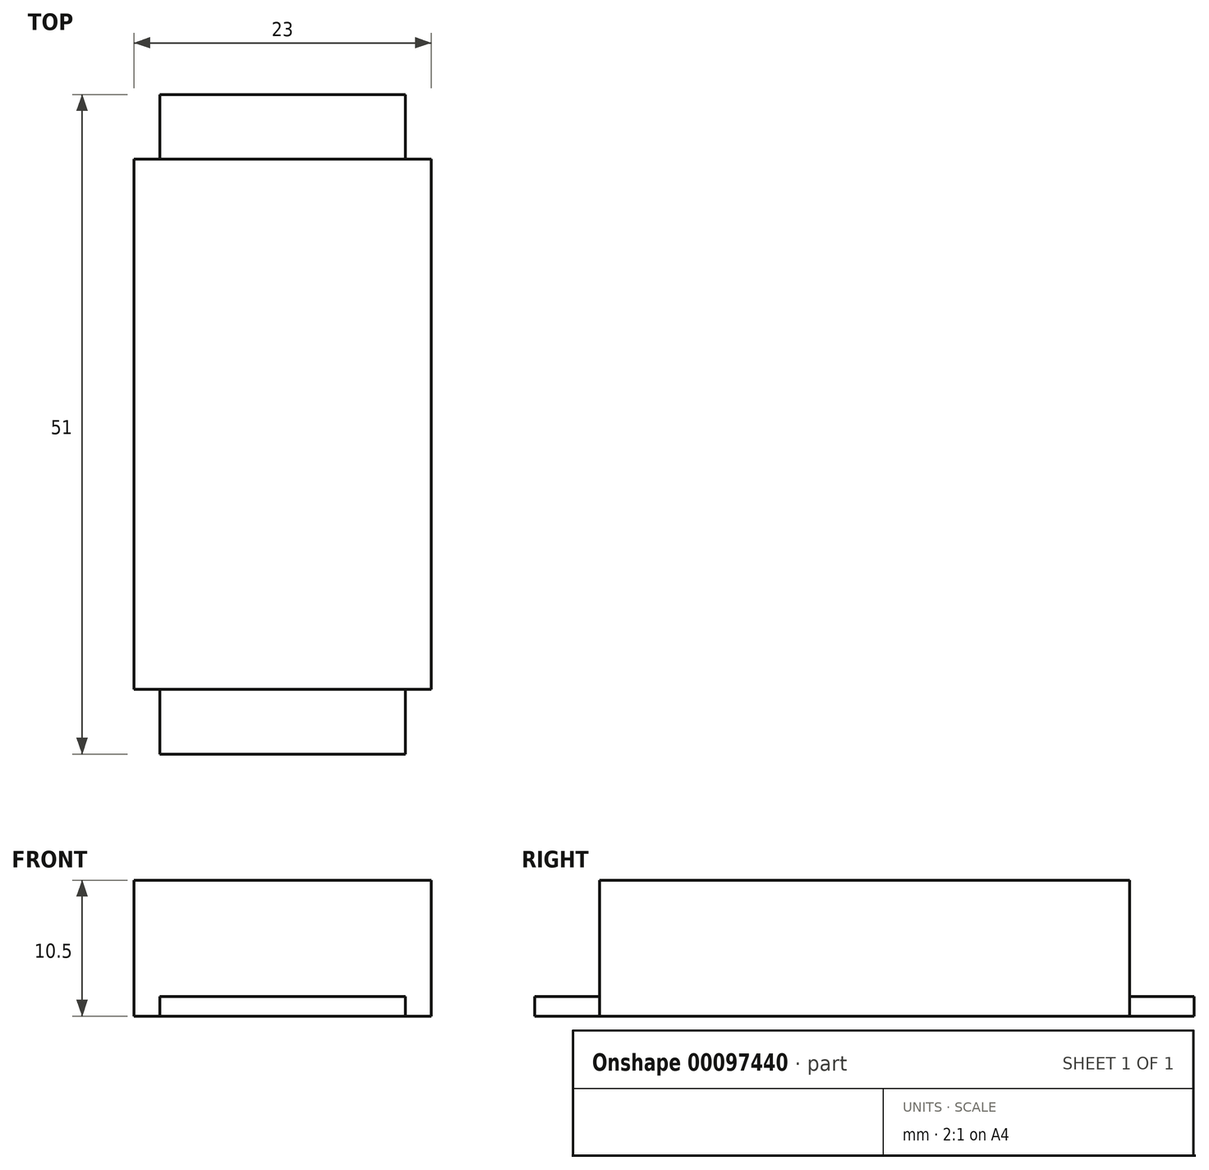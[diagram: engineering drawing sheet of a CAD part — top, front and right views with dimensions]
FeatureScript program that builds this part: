
annotation { "Feature Type Name" : "Feature", "Feature Type Description" : "" }
export const myFeature = defineFeature(function(context is Context, id is Id, definition is map)
    precondition{}
    {
        {
            var Q0;
            Q0=qCreatedBy(makeId("Top.planeOp"),FACE);
            var sketch = newSketch(context, id + "F0", { "sketchPlane" : qUnion([Q0])});
            skLineSegment(sketch, "E0.bottom", {"start": v(11.5, -20.5) * mm, "end": v(-11.5, -20.5) * mm});
            skLineSegment(sketch, "E0.top", {"start": v(11.5, 20.5) * mm, "end": v(-11.5, 20.5) * mm});
            skLineSegment(sketch, "E0.left", {"start": v(11.5, -20.5) * mm, "end": v(11.5, 20.5) * mm});
            skLineSegment(sketch, "E0.right", {"start": v(-11.5, -20.5) * mm, "end": v(-11.5, 20.5) * mm});
            skPoint(sketch, "E0.middle", {"position": v(0, 0) * mm});
            skLineSegment(sketch, "E1.bottom", {"start": v(9.5, 15.5) * mm, "end": v(-9.5, 15.5) * mm});
            skLineSegment(sketch, "E1.top", {"start": v(9.5, 25.5) * mm, "end": v(-9.5, 25.5) * mm});
            skLineSegment(sketch, "E1.left", {"start": v(9.5, 15.5) * mm, "end": v(9.5, 25.5) * mm});
            skLineSegment(sketch, "E1.right", {"start": v(-9.5, 15.5) * mm, "end": v(-9.5, 25.5) * mm});
            skPoint(sketch, "E1.middle", {"position": v(0, 20.5) * mm});
            skLineSegment(sketch, "E2.bottom", {"start": v(9.5, -25.5) * mm, "end": v(-9.5, -25.5) * mm});
            skLineSegment(sketch, "E2.top", {"start": v(9.5, -15.5) * mm, "end": v(-9.5, -15.5) * mm});
            skLineSegment(sketch, "E2.left", {"start": v(9.5, -25.5) * mm, "end": v(9.5, -15.5) * mm});
            skLineSegment(sketch, "E2.right", {"start": v(-9.5, -25.5) * mm, "end": v(-9.5, -15.5) * mm});
            skPoint(sketch, "E2.middle", {"position": v(0, -20.5) * mm});
            skSolve(sketch);
        }
        {
            var Q0;
            {var subQ3=sQuery(id+"F0.wireOp",EDGE,"E0.left");Q0=makeQuery(id+"F0.imprint","IMPRINT",FACE,{"disambiguationData":[TD([[makeQuery(id+"F0.imprint","IMPRINT",EDGE,{"derivedFrom":subQ3}),1.0]])]});}
            var Q1;
            {var subQ5=sQuery(id+"F0.wireOp",EDGE,"E1.bottom");Q1=makeQuery(id+"F0.imprint","IMPRINT",FACE,{"disambiguationData":[TD([[makeQuery(id+"F0.imprint","IMPRINT",EDGE,{"derivedFrom":subQ5}),-1.0]])]});}
            var Q2;
            {var subQ5=sQuery(id+"F0.wireOp",EDGE,"E2.top");Q2=makeQuery(id+"F0.imprint","IMPRINT",FACE,{"disambiguationData":[TD([[makeQuery(id+"F0.imprint","IMPRINT",EDGE,{"derivedFrom":subQ5}),1.0]])]});}
            extrude(context, id + "F1", {"entities" : qUnion([Q0, Q1, Q2]), "depth" : 9 * mm});
        }
        {
            var Q0;
            {var subQ5=sQuery(id+"F0.wireOp",EDGE,"E2.bottom");Q0=makeQuery(id+"F0.imprint","IMPRINT",FACE,{"disambiguationData":[TD([[makeQuery(id+"F0.imprint","IMPRINT",EDGE,{"derivedFrom":subQ5}),-1.0]])]});}
            var Q1;
            {var subQ5=sQuery(id+"F0.wireOp",EDGE,"E2.top");Q1=makeQuery(id+"F0.imprint","IMPRINT",FACE,{"disambiguationData":[TD([[makeQuery(id+"F0.imprint","IMPRINT",EDGE,{"derivedFrom":subQ5}),1.0]])]});}
            var Q2;
            {var subQ3=sQuery(id+"F0.wireOp",EDGE,"E0.left");Q2=makeQuery(id+"F0.imprint","IMPRINT",FACE,{"disambiguationData":[TD([[makeQuery(id+"F0.imprint","IMPRINT",EDGE,{"derivedFrom":subQ3}),1.0]])]});}
            var Q3;
            {var subQ5=sQuery(id+"F0.wireOp",EDGE,"E1.bottom");Q3=makeQuery(id+"F0.imprint","IMPRINT",FACE,{"disambiguationData":[TD([[makeQuery(id+"F0.imprint","IMPRINT",EDGE,{"derivedFrom":subQ5}),-1.0]])]});}
            var Q4;
            {var subQ5=sQuery(id+"F0.wireOp",EDGE,"E1.top");Q4=makeQuery(id+"F0.imprint","IMPRINT",FACE,{"disambiguationData":[TD([[makeQuery(id+"F0.imprint","IMPRINT",EDGE,{"derivedFrom":subQ5}),1.0]])]});}
            extrude(context, id + "F2", {"entities" : qUnion([Q0, Q1, Q2, Q3, Q4]), "operationType" : NewBodyOperationType.ADD, "oppositeDirection" : true, "depth" : 1.5 * mm});
        }
    });
